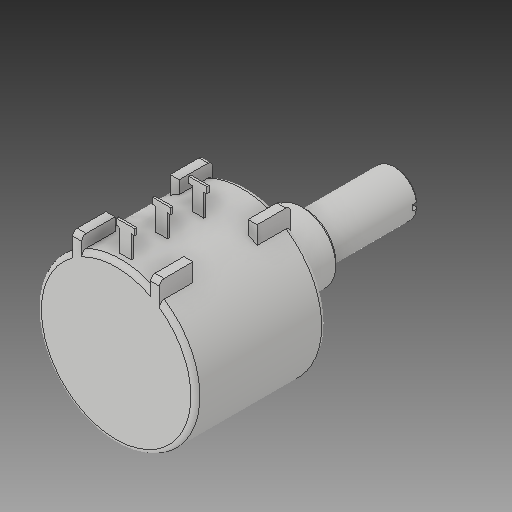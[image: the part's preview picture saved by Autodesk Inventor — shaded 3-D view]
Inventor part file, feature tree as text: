
AUTODESK INVENTOR PART (.ipt)
format: ipt  version: 2018 (Build 220112000, 112)  size: 214,016 bytes
history: native  units: in
note: dims shown in document units (in); Inventor stores cm internally (conversion verified against a paired STEP export)
features: fillet x1
ambient origin geometry x8: Origin, YZ Plane, XZ Plane, XY Plane, X Axis, Y Axis, Z Axis, Center Point
bodies: Solid1 (feature_tree)
feature tree (1):
  fillet  "Fillet1"  [1 undecoded]
note: 1 required parameter value undecoded (feature->parameter linkage not recoverable at this tier; creation-order binding heuristic only, values carry confidence <= 0.55)
